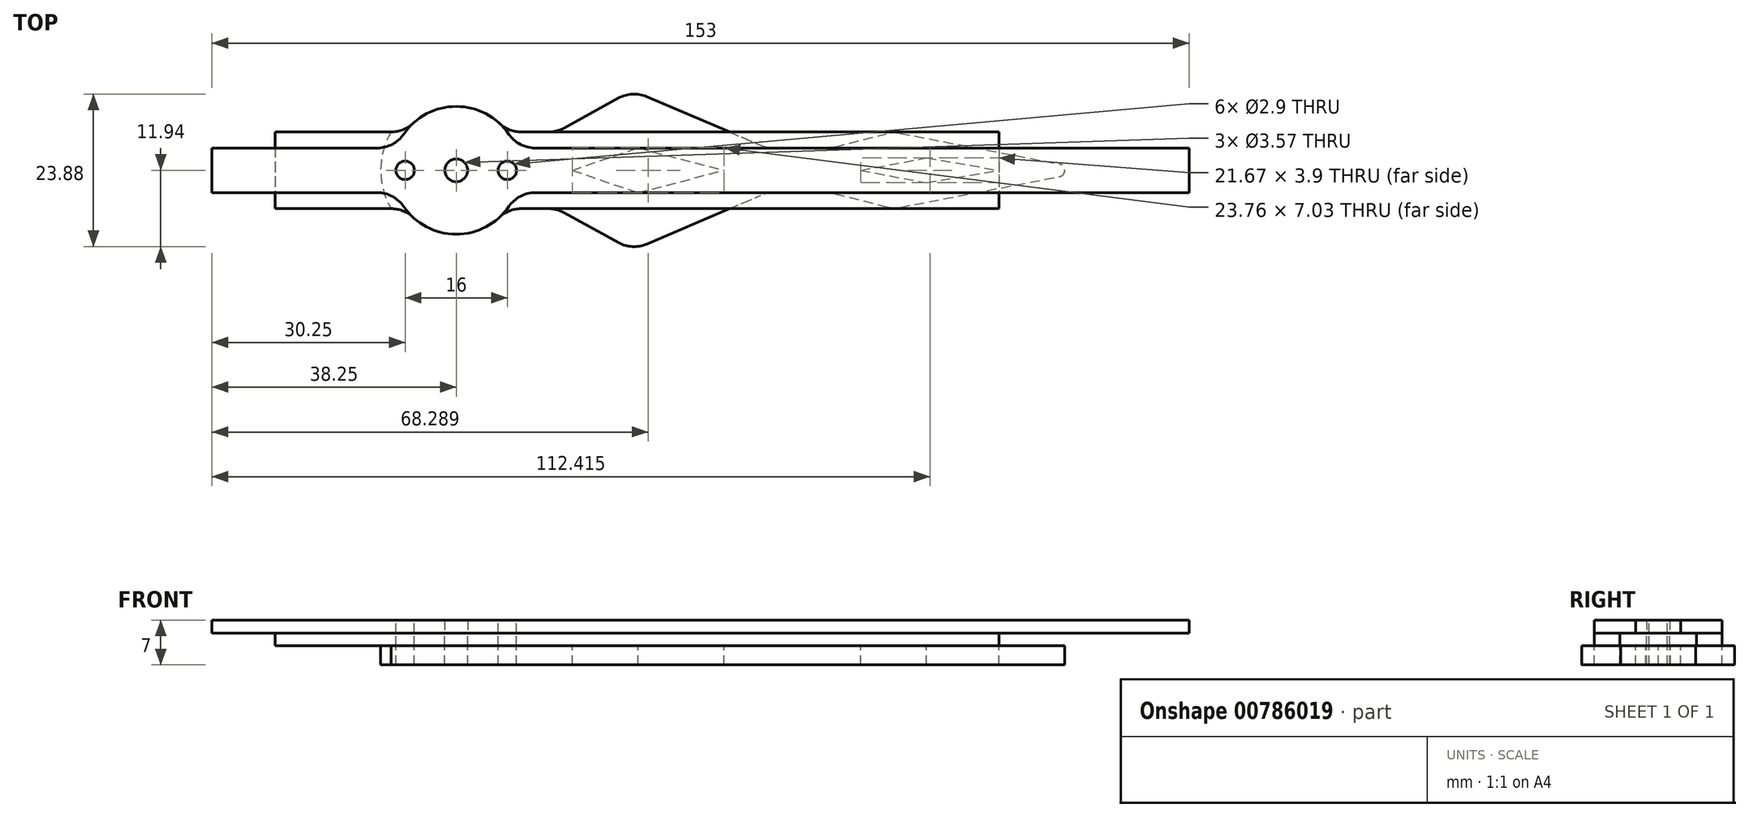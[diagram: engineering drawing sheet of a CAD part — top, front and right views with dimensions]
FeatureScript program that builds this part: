
annotation { "Feature Type Name" : "Feature", "Feature Type Description" : "" }
export const myFeature = defineFeature(function(context is Context, id is Id, definition is map)
    precondition{}
    {
        {
            var Q0;
            Q0=qCreatedBy(makeId("Top.planeOp"),FACE);
            var sketch = newSketch(context, id + "F0", { "sketchPlane" : qUnion([Q0])});
            skCircle(sketch, "E0", {"center": v(0, 0) * mm, "radius": 1.79 * mm});
            skLineSegment(sketch, "E1.bottom", {"start": v(-38.25, 3.5) * mm, "end": v(114.75, 3.5) * mm});
            skLineSegment(sketch, "E1.top", {"start": v(-38.25, -3.5) * mm, "end": v(114.75, -3.5) * mm});
            skLineSegment(sketch, "E1.left", {"start": v(-38.25, 3.5) * mm, "end": v(-38.25, -3.5) * mm});
            skLineSegment(sketch, "E1.right", {"start": v(114.75, 3.5) * mm, "end": v(114.75, -3.5) * mm});
            skCircle(sketch, "E2", {"center": v(0, 0) * mm, "radius": 10 * mm});
            skSolve(sketch);
        }
        {
            var Q0;
            Q0=qSketchRegion(id+"F0",true);
            extrude(context, id + "F1", {"entities" : qUnion([Q0]), "depth" : 2 * mm});
        }
        {
            var Q0;
            Q0=qCreatedBy(makeId("Top.planeOp"),FACE);
            var sketch = newSketch(context, id + "F2", { "sketchPlane" : qUnion([Q0])});
            skCircle(sketch, "E3", {"center": v(0, 0) * mm, "radius": 1.79 * mm});
            skLineSegment(sketch, "E4.bottom", {"start": v(-28.33, 6) * mm, "end": v(85, 6) * mm});
            skLineSegment(sketch, "E4.top", {"start": v(-28.33, -6) * mm, "end": v(85, -6) * mm});
            skLineSegment(sketch, "E4.left", {"start": v(-28.33, 6) * mm, "end": v(-28.33, -6) * mm});
            skLineSegment(sketch, "E4.right", {"start": v(85, 6) * mm, "end": v(85, -6) * mm});
            skCircle(sketch, "E5", {"center": v(0, 0) * mm, "radius": 10 * mm});
            skSolve(sketch);
        }
        {
            var Q0;
            Q0=qSketchRegion(id+"F2",true);
            extrude(context, id + "F3", {"entities" : qUnion([Q0]), "oppositeDirection" : true, "depth" : 2 * mm});
        }
        {
            var Q0;
            Q0=makeQuery(id+"F1.opExtrude","CAP_FACE",FACE,{"disambiguationData":[OSD([sQuery(id+"F0.wireOp",EDGE,"E0"),sQuery(id+"F0.wireOp",EDGE,"E1.bottom"),sQuery(id+"F0.wireOp",EDGE,"E1.top"),sQuery(id+"F0.wireOp",EDGE,"E1.left"),sQuery(id+"F0.wireOp",EDGE,"E1.right"),sQuery(id+"F0.wireOp",EDGE,"E2")])],"isStart":false});
            var sketch = newSketch(context, id + "F4", { "sketchPlane" : qUnion([Q0])});
            skCircle(sketch, "E6", {"center": v(8, 0) * mm, "radius": 1.45 * mm});
            skLineSegment(sketch, "E7", {"start": v(0, 0) * mm, "end": v(16, 0) * mm, "construction": true});
            skLineSegment(sketch, "E8", {"start": v(0, 0) * mm, "end": v(0, 19.04) * mm, "construction": true});
            skCircle(sketch, "E9.MirrorC", {"center": v(-8, 0) * mm, "radius": 1.45 * mm});
            skSolve(sketch);
        }
        {
            var Q0;
            Q0=qSketchRegion(id+"F4",true);
            extrude(context, id + "F5", {"entities" : qUnion([Q0]), "operationType" : NewBodyOperationType.REMOVE, "oppositeDirection" : true, "depth" : 25 * mm, "offsetDistance" : 25 * mm});
        }
        {
            var Q0;
            {var subQ0=sQuery(id+"F0.wireOp",EDGE,"E2");var subQ1=sQuery(id+"F0.wireOp",EDGE,"E1.top");Q0=makeQuery(id+"F1.opExtrude","SWEPT_EDGE",EDGE,{"disambiguationData":[OSD([subQ1,subQ0]),TDD([makeQuery(id+"F0.imprint","INTERSECT",VERTEX,{"disambiguationData":[OD(1.0)],"derivedFrom":[subQ1,subQ0]})])]});}
            var Q1;
            {var subQ0=sQuery(id+"F0.wireOp",EDGE,"E2");var subQ1=sQuery(id+"F0.wireOp",EDGE,"E1.bottom");Q1=makeQuery(id+"F1.opExtrude","SWEPT_EDGE",EDGE,{"disambiguationData":[OSD([subQ1,subQ0]),TDD([makeQuery(id+"F0.imprint","INTERSECT",VERTEX,{"disambiguationData":[OD(1.0)],"derivedFrom":[subQ1,subQ0]})])]});}
            var Q2;
            {var subQ0=sQuery(id+"F0.wireOp",EDGE,"E2");var subQ1=sQuery(id+"F0.wireOp",EDGE,"E1.bottom");Q2=makeQuery(id+"F1.opExtrude","SWEPT_EDGE",EDGE,{"disambiguationData":[OSD([subQ1,subQ0]),TDD([makeQuery(id+"F0.imprint","INTERSECT",VERTEX,{"disambiguationData":[OD(0.0)],"derivedFrom":[subQ1,subQ0]})])]});}
            var Q3;
            {var subQ0=sQuery(id+"F0.wireOp",EDGE,"E2");var subQ1=sQuery(id+"F0.wireOp",EDGE,"E1.top");Q3=makeQuery(id+"F1.opExtrude","SWEPT_EDGE",EDGE,{"disambiguationData":[OSD([subQ1,subQ0]),TDD([makeQuery(id+"F0.imprint","INTERSECT",VERTEX,{"disambiguationData":[OD(0.0)],"derivedFrom":[subQ1,subQ0]})])]});}
            var Q4;
            {var subQ0=sQuery(id+"F2.wireOp",EDGE,"E5");var subQ1=sQuery(id+"F2.wireOp",EDGE,"E4.top");Q4=makeQuery(id+"F3.opExtrude","SWEPT_EDGE",EDGE,{"disambiguationData":[OSD([subQ1,subQ0]),TDD([makeQuery(id+"F2.imprint","INTERSECT",VERTEX,{"disambiguationData":[OD(0.0)],"derivedFrom":[subQ1,subQ0]})])]});}
            var Q5;
            {var subQ0=sQuery(id+"F2.wireOp",EDGE,"E5");var subQ1=sQuery(id+"F2.wireOp",EDGE,"E4.bottom");Q5=makeQuery(id+"F3.opExtrude","SWEPT_EDGE",EDGE,{"disambiguationData":[OSD([subQ1,subQ0]),TDD([makeQuery(id+"F2.imprint","INTERSECT",VERTEX,{"disambiguationData":[OD(1.0)],"derivedFrom":[subQ1,subQ0]})])]});}
            var Q6;
            {var subQ0=sQuery(id+"F2.wireOp",EDGE,"E5");var subQ1=sQuery(id+"F2.wireOp",EDGE,"E4.top");Q6=makeQuery(id+"F3.opExtrude","SWEPT_EDGE",EDGE,{"disambiguationData":[OSD([subQ1,subQ0]),TDD([makeQuery(id+"F2.imprint","INTERSECT",VERTEX,{"disambiguationData":[OD(1.0)],"derivedFrom":[subQ1,subQ0]})])]});}
            var Q7;
            {var subQ0=sQuery(id+"F2.wireOp",EDGE,"E5");var subQ1=sQuery(id+"F2.wireOp",EDGE,"E4.bottom");Q7=makeQuery(id+"F3.opExtrude","SWEPT_EDGE",EDGE,{"disambiguationData":[OSD([subQ1,subQ0]),TDD([makeQuery(id+"F2.imprint","INTERSECT",VERTEX,{"disambiguationData":[OD(0.0)],"derivedFrom":[subQ1,subQ0]})])]});}
            fillet(context, id + "F6", {"entities" : qUnion([Q0, Q1, Q2, Q3, Q4, Q5, Q6, Q7]), "radius" : 5 * mm, "tangentPropagation" : true, "allowEdgeOverflow" : false});
        }
        {
            var Q0;
            Q0=makeQuery(id+"F3.opExtrude","CAP_FACE",FACE,{"disambiguationData":[OSD([sQuery(id+"F2.wireOp",EDGE,"E3"),sQuery(id+"F2.wireOp",EDGE,"E4.bottom"),sQuery(id+"F2.wireOp",EDGE,"E4.top"),sQuery(id+"F2.wireOp",EDGE,"E4.left"),sQuery(id+"F2.wireOp",EDGE,"E4.right"),sQuery(id+"F2.wireOp",EDGE,"E5")])],"isStart":false});
            var sketch = newSketch(context, id + "F7", { "sketchPlane" : qUnion([Q0])});
            skLineSegment(sketch, "E10", {"start": v(18.16, 0) * mm, "end": v(28.48, 3.51) * mm});
            skLineSegment(sketch, "E11", {"start": v(28.48, 3.51) * mm, "end": v(41.92, 0) * mm});
            skLineSegment(sketch, "E12", {"start": v(63.33, 0) * mm, "end": v(73.64, 1.95) * mm});
            skLineSegment(sketch, "E13", {"start": v(73.64, 1.95) * mm, "end": v(85, 0) * mm});
            skLineSegment(sketch, "E14", {"start": v(0, 0) * mm, "end": v(85, 0) * mm, "construction": true});
            skCircle(sketch, "E15", {"center": v(0, 0) * mm, "radius": 11.83 * mm});
            skLineSegment(sketch, "E16.bottom", {"start": v(-10.2, 6) * mm, "end": v(-28.33, 6) * mm});
            skLineSegment(sketch, "E16.top", {"start": v(-10.2, -6) * mm, "end": v(-28.33, -6) * mm});
            skLineSegment(sketch, "E16.left", {"start": v(-10.2, 6) * mm, "end": v(-10.2, -6) * mm});
            skLineSegment(sketch, "E16.right", {"start": v(-28.33, 6) * mm, "end": v(-28.33, -6) * mm});
            skCircle(sketch, "E17", {"center": v(0, 0) * mm, "radius": 1.79 * mm});
            skCircle(sketch, "E18", {"center": v(8, 0) * mm, "radius": 1.45 * mm});
            skCircle(sketch, "E19", {"center": v(-8, 0) * mm, "radius": 1.45 * mm});
            skLineSegment(sketch, "E20", {"start": v(15.74, 6) * mm, "end": v(27.57, 12.5) * mm});
            skLineSegment(sketch, "E21", {"start": v(27.57, 12.5) * mm, "end": v(48.65, 3.5) * mm});
            skLineSegment(sketch, "E22", {"start": v(48.65, 3.5) * mm, "end": v(58.72, 3.5) * mm});
            skLineSegment(sketch, "E23", {"start": v(58.72, 3.5) * mm, "end": v(68.44, 6) * mm});
            skLineSegment(sketch, "E24", {"start": v(68.44, 6) * mm, "end": v(99.58, 0) * mm});
            skLineSegment(sketch, "E25", {"start": v(15.74, 6) * mm, "end": v(10.2, 6) * mm});
            skLineSegment(sketch, "E26", {"start": v(11.83, 0) * mm, "end": v(18.16, 0) * mm});
            skLineSegment(sketch, "E27", {"start": v(41.92, 0) * mm, "end": v(63.33, 0) * mm});
            skLineSegment(sketch, "E28.MirrorCS", {"start": v(28.48, -3.51) * mm, "end": v(41.92, 0) * mm});
            skLineSegment(sketch, "E29.MirrorCS", {"start": v(18.16, 0) * mm, "end": v(28.48, -3.51) * mm});
            skLineSegment(sketch, "E30.MirrorCS", {"start": v(15.74, -6) * mm, "end": v(27.57, -12.5) * mm});
            skLineSegment(sketch, "E31.MirrorCS", {"start": v(27.57, -12.5) * mm, "end": v(48.65, -3.5) * mm});
            skLineSegment(sketch, "E32.MirrorCS", {"start": v(48.65, -3.5) * mm, "end": v(58.72, -3.5) * mm});
            skLineSegment(sketch, "E33.MirrorCS", {"start": v(58.72, -3.5) * mm, "end": v(68.44, -6) * mm});
            skLineSegment(sketch, "E34.MirrorCS", {"start": v(68.44, -6) * mm, "end": v(99.58, 0) * mm});
            skLineSegment(sketch, "E35.MirrorCS", {"start": v(63.33, 0) * mm, "end": v(73.64, -1.95) * mm});
            skLineSegment(sketch, "E36.MirrorCS", {"start": v(73.64, -1.95) * mm, "end": v(85, 0) * mm});
            skLineSegment(sketch, "E37.MirrorCS", {"start": v(15.74, -6) * mm, "end": v(10.2, -6) * mm});
            skSolve(sketch);
        }
        {
            var Q0;
            {var subQ1=sQuery(id+"F2.wireOp",EDGE,"E5");var subQ2=sQuery(id+"F2.wireOp",EDGE,"E4.top");var subQ4=makeQuery(id+"F2.imprint","INTERSECT",VERTEX,{"disambiguationData":[OD(0.0)],"derivedFrom":[subQ2,subQ1]});Q0=makeQuery(id+"F7.imprint","IMPRINT",FACE,{"disambiguationData":[TD([[makeQuery(id+"F7.imprint","IMPRINT",EDGE,{"derivedFrom":makeQuery(id+"F3.opExtrude","CAP_EDGE",EDGE,{"disambiguationData":[OSD([subQ1]),TDD([makeQuery(id+"F2.imprint","IMPRINT",EDGE,{"disambiguationData":[TD([[subQ4,-1.0]])],"derivedFrom":subQ1})])],"isStart":false})}),1.0]])]});}
            var Q1;
            {var subQ1=sQuery(id+"F2.wireOp",EDGE,"E5");var subQ2=sQuery(id+"F2.wireOp",EDGE,"E4.bottom");var subQ4=makeQuery(id+"F2.imprint","INTERSECT",VERTEX,{"disambiguationData":[OD(0.0)],"derivedFrom":[subQ2,subQ1]});Q1=makeQuery(id+"F7.imprint","IMPRINT",FACE,{"disambiguationData":[TD([[makeQuery(id+"F7.imprint","IMPRINT",EDGE,{"derivedFrom":makeQuery(id+"F3.opExtrude","CAP_EDGE",EDGE,{"disambiguationData":[OSD([subQ1]),TDD([makeQuery(id+"F2.imprint","IMPRINT",EDGE,{"disambiguationData":[TD([[subQ4,1.0]])],"derivedFrom":subQ1})])],"isStart":false})}),1.0]])]});}
            var Q2;
            {var subQ0=sQuery(id+"F7.wireOp",EDGE,"E16.left");Q2=makeQuery(id+"F7.imprint","IMPRINT",FACE,{"disambiguationData":[TD([[makeQuery(id+"F7.imprint","IMPRINT",EDGE,{"derivedFrom":subQ0}),-1.0]])]});}
            var Q3;
            Q3=makeQuery(id+"F7.imprint","IMPRINT",FACE,{"disambiguationData":[TD([[makeQuery(id+"F7.imprint","IMPRINT",EDGE,{"derivedFrom":sQuery(id+"F7.wireOp",EDGE,"E16.left")}),1.0]])]});
            var Q4;
            {var subQ0=sQuery(id+"F7.wireOp",EDGE,"E20");Q4=makeQuery(id+"F7.imprint","IMPRINT",FACE,{"disambiguationData":[TD([[makeQuery(id+"F7.imprint","IMPRINT",EDGE,{"derivedFrom":subQ0}),-1.0]])]});}
            var Q5;
            {var subQ0=sQuery(id+"F7.wireOp",EDGE,"E30.MirrorCS");Q5=makeQuery(id+"F7.imprint","IMPRINT",FACE,{"disambiguationData":[TD([[makeQuery(id+"F7.imprint","IMPRINT",EDGE,{"derivedFrom":subQ0}),1.0]])]});}
            var Q6;
            {var subQ0=sQuery(id+"F7.wireOp",EDGE,"E34.MirrorCS");var subQ1=sQuery(id+"F7.wireOp",EDGE,"E24");var subQ2=makeQuery(id+"F7.imprint","INTERSECT",VERTEX,{"derivedFrom":[subQ1,subQ0]});Q6=makeQuery(id+"F7.imprint","IMPRINT",FACE,{"disambiguationData":[TD([[makeQuery(id+"F7.imprint","IMPRINT",EDGE,{"disambiguationData":[TD([[subQ2,1.0]])],"derivedFrom":subQ1}),-1.0]])]});}
            var Q7;
            Q7=makeQuery(id+"F7.imprint","IMPRINT",FACE,{"disambiguationData":[TD([[makeQuery(id+"F7.imprint","IMPRINT",EDGE,{"derivedFrom":sQuery(id+"F7.wireOp",EDGE,"E10")}),1.0]])]});
            var Q8;
            {var subQ12=sQuery(id+"F7.wireOp",EDGE,"E26");Q8=makeQuery(id+"F7.imprint","IMPRINT",FACE,{"disambiguationData":[TD([[makeQuery(id+"F7.imprint","IMPRINT",EDGE,{"derivedFrom":subQ12}),-1.0]])]});}
            extrude(context, id + "F8", {"entities" : qUnion([Q0, Q1, Q2, Q3, Q4, Q5, Q6, Q7, Q8]), "depth" : 3 * mm, "offsetDistance" : 25 * mm});
        }
        {
            var Q0;
            Q0=makeQuery(id+"F8.opExtrude","SWEPT_EDGE",EDGE,{"disambiguationData":[OSD([sQuery(id+"F2.wireOp",EDGE,"E3"),sQuery(id+"F2.wireOp",EDGE,"E4.bottom"),sQuery(id+"F2.wireOp",EDGE,"E4.top"),sQuery(id+"F2.wireOp",EDGE,"E4.left"),sQuery(id+"F2.wireOp",EDGE,"E4.right"),sQuery(id+"F2.wireOp",EDGE,"E5"),sQuery(id+"F7.wireOp",EDGE,"E15"),sQuery(id+"F7.wireOp",EDGE,"E37.MirrorCS")])]});
            var Q1;
            Q1=makeQuery(id+"F8.opExtrude","SWEPT_EDGE",EDGE,{"disambiguationData":[OSD([sQuery(id+"F2.wireOp",EDGE,"E4.bottom"),sQuery(id+"F7.wireOp",EDGE,"E30.MirrorCS"),sQuery(id+"F7.wireOp",EDGE,"E37.MirrorCS")])]});
            var Q2;
            Q2=makeQuery(id+"F8.opExtrude","SWEPT_EDGE",EDGE,{"disambiguationData":[OSD([sQuery(id+"F2.wireOp",EDGE,"E3"),sQuery(id+"F2.wireOp",EDGE,"E4.bottom"),sQuery(id+"F2.wireOp",EDGE,"E4.top"),sQuery(id+"F2.wireOp",EDGE,"E4.left"),sQuery(id+"F2.wireOp",EDGE,"E4.right"),sQuery(id+"F2.wireOp",EDGE,"E5"),sQuery(id+"F7.wireOp",EDGE,"E15"),sQuery(id+"F7.wireOp",EDGE,"E25")])]});
            var Q3;
            Q3=makeQuery(id+"F8.opExtrude","SWEPT_EDGE",EDGE,{"disambiguationData":[OSD([sQuery(id+"F2.wireOp",EDGE,"E4.top"),sQuery(id+"F7.wireOp",EDGE,"E20"),sQuery(id+"F7.wireOp",EDGE,"E25")])]});
            var Q4;
            Q4=makeQuery(id+"F8.opExtrude","SWEPT_EDGE",EDGE,{"disambiguationData":[OSD([sQuery(id+"F7.wireOp",EDGE,"E20"),sQuery(id+"F7.wireOp",EDGE,"E21")])]});
            var Q5;
            Q5=makeQuery(id+"F8.opExtrude","SWEPT_EDGE",EDGE,{"disambiguationData":[OSD([sQuery(id+"F7.wireOp",EDGE,"E30.MirrorCS"),sQuery(id+"F7.wireOp",EDGE,"E31.MirrorCS")])]});
            var Q6;
            Q6=makeQuery(id+"F8.opExtrude","SWEPT_EDGE",EDGE,{"disambiguationData":[OSD([sQuery(id+"F7.wireOp",EDGE,"E31.MirrorCS"),sQuery(id+"F7.wireOp",EDGE,"E32.MirrorCS")])]});
            var Q7;
            Q7=makeQuery(id+"F8.opExtrude","SWEPT_EDGE",EDGE,{"disambiguationData":[OSD([sQuery(id+"F7.wireOp",EDGE,"E32.MirrorCS"),sQuery(id+"F7.wireOp",EDGE,"E33.MirrorCS")])]});
            var Q8;
            Q8=makeQuery(id+"F8.opExtrude","SWEPT_EDGE",EDGE,{"disambiguationData":[OSD([sQuery(id+"F2.wireOp",EDGE,"E4.bottom"),sQuery(id+"F7.wireOp",EDGE,"E33.MirrorCS"),sQuery(id+"F7.wireOp",EDGE,"E34.MirrorCS")])]});
            var Q9;
            Q9=makeQuery(id+"F8.opExtrude","SWEPT_EDGE",EDGE,{"disambiguationData":[OSD([sQuery(id+"F7.wireOp",EDGE,"E21"),sQuery(id+"F7.wireOp",EDGE,"E22")])]});
            var Q10;
            Q10=makeQuery(id+"F8.opExtrude","SWEPT_EDGE",EDGE,{"disambiguationData":[OSD([sQuery(id+"F7.wireOp",EDGE,"E22"),sQuery(id+"F7.wireOp",EDGE,"E23")])]});
            var Q11;
            Q11=makeQuery(id+"F8.opExtrude","SWEPT_EDGE",EDGE,{"disambiguationData":[OSD([sQuery(id+"F2.wireOp",EDGE,"E4.top"),sQuery(id+"F7.wireOp",EDGE,"E23"),sQuery(id+"F7.wireOp",EDGE,"E24")])]});
            fillet(context, id + "F9", {"entities" : qUnion([Q0, Q1, Q2, Q3, Q4, Q5, Q6, Q7, Q8, Q9, Q10, Q11]), "radius" : 5 * mm, "tangentPropagation" : true, "allowEdgeOverflow" : false});
        }
        {
            var Q0;
            Q0=makeQuery(id+"F8.opExtrude","SWEPT_EDGE",EDGE,{"disambiguationData":[OSD([sQuery(id+"F7.wireOp",EDGE,"E24"),sQuery(id+"F7.wireOp",EDGE,"E34.MirrorCS")])]});
            fillet(context, id + "F10", {"entities" : qUnion([Q0]), "radius" : 1 * mm, "tangentPropagation" : true, "allowEdgeOverflow" : false});
        }
    });
